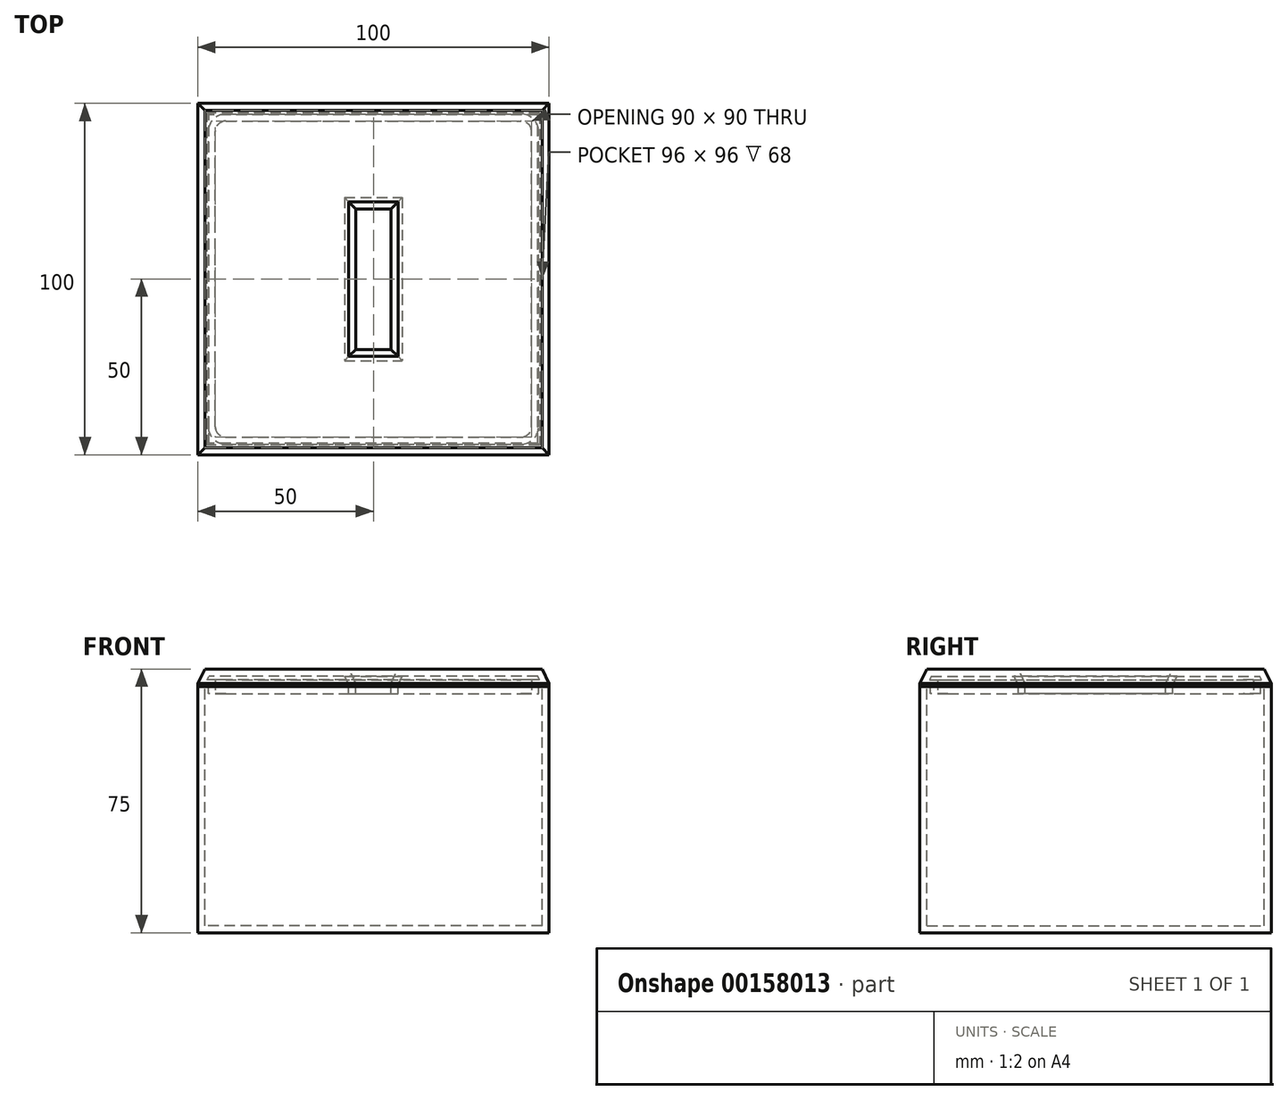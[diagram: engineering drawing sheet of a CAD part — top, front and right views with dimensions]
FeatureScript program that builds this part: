
annotation { "Feature Type Name" : "Feature", "Feature Type Description" : "" }
export const myFeature = defineFeature(function(context is Context, id is Id, definition is map)
    precondition{}
    {
        {
            var Q0;
            Q0=qCreatedBy(makeId("Top.planeOp"),FACE);
            var sketch = newSketch(context, id + "F0", { "sketchPlane" : qUnion([Q0])});
            skLineSegment(sketch, "E0.bottom", {"start": v(50, -50) * mm, "end": v(-50, -50) * mm});
            skLineSegment(sketch, "E0.top", {"start": v(50, 50) * mm, "end": v(-50, 50) * mm});
            skLineSegment(sketch, "E0.left", {"start": v(50, -50) * mm, "end": v(50, 50) * mm});
            skLineSegment(sketch, "E0.right", {"start": v(-50, -50) * mm, "end": v(-50, 50) * mm});
            skPoint(sketch, "E0.middle", {"position": v(0, 0) * mm});
            skSolve(sketch);
        }
        {
            var Q0;
            Q0=makeQuery(id+"F0.imprint","IMPRINT",FACE,{"disambiguationData":[TD([[makeQuery(id+"F0.imprint","IMPRINT",EDGE,{"derivedFrom":sQuery(id+"F0.wireOp",EDGE,"E0.bottom")}),-1.0]])]});
            extrude(context, id + "F1", {"entities" : qUnion([Q0]), "depth" : 70 * mm});
        }
        {
            var Q0;
            Q0=makeQuery(id+"F1.opExtrude","CAP_FACE",FACE,{"disambiguationData":[OSD([sQuery(id+"F0.wireOp",EDGE,"E0.bottom"),sQuery(id+"F0.wireOp",EDGE,"E0.top"),sQuery(id+"F0.wireOp",EDGE,"E0.left"),sQuery(id+"F0.wireOp",EDGE,"E0.right")])],"isStart":false});
            var sketch = newSketch(context, id + "F2", { "sketchPlane" : qUnion([Q0])});
            skLineSegment(sketch, "E1.bottom", {"start": v(48, -48) * mm, "end": v(-48, -48) * mm});
            skLineSegment(sketch, "E1.top", {"start": v(48, 48) * mm, "end": v(-48, 48) * mm});
            skLineSegment(sketch, "E1.left", {"start": v(48, -48) * mm, "end": v(48, 48) * mm});
            skLineSegment(sketch, "E1.right", {"start": v(-48, -48) * mm, "end": v(-48, 48) * mm});
            skPoint(sketch, "E1.middle", {"position": v(0, 0) * mm});
            skSolve(sketch);
        }
        {
            var Q0;
            Q0=makeQuery(id+"F2.imprint","IMPRINT",FACE,{"disambiguationData":[TD([[makeQuery(id+"F2.imprint","IMPRINT",EDGE,{"derivedFrom":sQuery(id+"F2.wireOp",EDGE,"E1.bottom")}),-1.0]])]});
            extrude(context, id + "F3", {"entities" : qUnion([Q0]), "operationType" : NewBodyOperationType.REMOVE, "oppositeDirection" : true, "depth" : 68 * mm});
        }
        {
            var Q0;
            Q0=makeQuery(id+"F1.opExtrude","CAP_FACE",FACE,{"disambiguationData":[OSD([sQuery(id+"F0.wireOp",EDGE,"E0.bottom"),sQuery(id+"F0.wireOp",EDGE,"E0.top"),sQuery(id+"F0.wireOp",EDGE,"E0.left"),sQuery(id+"F0.wireOp",EDGE,"E0.right")])],"isStart":false});
            var sketch = newSketch(context, id + "F4", { "sketchPlane" : qUnion([Q0])});
            skLineSegment(sketch, "E2.0", {"start": v(-50, -50) * mm, "end": v(-50, 50) * mm});
            skLineSegment(sketch, "E3.0", {"start": v(50, 50) * mm, "end": v(-50, 50) * mm});
            skLineSegment(sketch, "E3.1", {"start": v(50, -50) * mm, "end": v(50, 50) * mm});
            skLineSegment(sketch, "E3.2", {"start": v(50, -50) * mm, "end": v(-50, -50) * mm});
            skSolve(sketch);
        }
        {
            var Q0;
            Q0 = qSketchRegion(id + "F4", true);
            extrude(context, id + "F5", {"entities" : qUnion([Q0]), "depth" : 5 * mm});
        }
        {
            var Q0;
            Q0=makeQuery(id+"F5.opExtrude","CAP_FACE",FACE,{"disambiguationData":[OSD([sQuery(id+"F4.wireOp",EDGE,"E2.0"),sQuery(id+"F4.wireOp",EDGE,"E3.0"),sQuery(id+"F4.wireOp",EDGE,"E3.1"),sQuery(id+"F4.wireOp",EDGE,"E3.2")])],"isStart":true});
            var sketch = newSketch(context, id + "F6", { "sketchPlane" : qUnion([Q0])});
            skLineSegment(sketch, "E4.1", {"start": v(-48, 48) * mm, "end": v(-48, -48) * mm, "construction": true});
            skLineSegment(sketch, "E4.2", {"start": v(48, -48) * mm, "end": v(-48, -48) * mm, "construction": true});
            skLineSegment(sketch, "E4.3", {"start": v(48, 48) * mm, "end": v(48, -48) * mm, "construction": true});
            skLineSegment(sketch, "E4.4", {"start": v(48, 48) * mm, "end": v(-48, 48) * mm, "construction": true});
            skLineSegment(sketch, "E5.bottom", {"start": v(-47, 47) * mm, "end": v(47, 47) * mm});
            skLineSegment(sketch, "E5.top", {"start": v(-47, -47) * mm, "end": v(47, -47) * mm});
            skLineSegment(sketch, "E5.left", {"start": v(-47, 47) * mm, "end": v(-47, -47) * mm});
            skLineSegment(sketch, "E5.right", {"start": v(47, 47) * mm, "end": v(47, -47) * mm});
            skPoint(sketch, "E5.middle", {"position": v(0, 0) * mm});
            skSolve(sketch);
        }
        {
            var Q0;
            Q0=makeQuery(id+"F6.imprint","IMPRINT",FACE,{"disambiguationData":[TD([[makeQuery(id+"F6.imprint","IMPRINT",EDGE,{"derivedFrom":sQuery(id+"F6.wireOp",EDGE,"E5.bottom")}),-1.0]])]});
            extrude(context, id + "F7", {"entities" : qUnion([Q0]), "operationType" : NewBodyOperationType.ADD, "depth" : 2 * mm});
        }
        {
            var Q0;
            Q0=makeQuery(id+"F5.opExtrude","CAP_FACE",FACE,{"disambiguationData":[OSD([sQuery(id+"F4.wireOp",EDGE,"E2.0"),sQuery(id+"F4.wireOp",EDGE,"E3.0"),sQuery(id+"F4.wireOp",EDGE,"E3.1"),sQuery(id+"F4.wireOp",EDGE,"E3.2")])],"isStart":false});
            var sketch = newSketch(context, id + "F8", { "sketchPlane" : qUnion([Q0])});
            skLineSegment(sketch, "E6.bottom", {"start": v(5, -20) * mm, "end": v(-5, -20) * mm});
            skLineSegment(sketch, "E6.top", {"start": v(5, 20) * mm, "end": v(-5, 20) * mm});
            skLineSegment(sketch, "E6.left", {"start": v(5, -20) * mm, "end": v(5, 20) * mm});
            skLineSegment(sketch, "E6.right", {"start": v(-5, -20) * mm, "end": v(-5, 20) * mm});
            skPoint(sketch, "E6.middle", {"position": v(0, 0) * mm});
            skSolve(sketch);
        }
        {
            var Q0;
            Q0=makeQuery(id+"F8.imprint","IMPRINT",FACE,{"disambiguationData":[TD([[makeQuery(id+"F8.imprint","IMPRINT",EDGE,{"derivedFrom":sQuery(id+"F8.wireOp",EDGE,"E6.bottom")}),-1.0]])]});
            extrude(context, id + "F9", {"entities" : qUnion([Q0]), "operationType" : NewBodyOperationType.REMOVE, "oppositeDirection" : true, "depth" : 25 * mm});
        }
        {
            var Q0;
            Q0=makeQuery(id+"F7.opExtrude","SWEPT_EDGE",EDGE,{"disambiguationData":[OSD([sQuery(id+"F6.wireOp",EDGE,"E5.bottom"),sQuery(id+"F6.wireOp",EDGE,"E5.left")])]});
            var Q1;
            Q1=makeQuery(id+"F7.opExtrude","SWEPT_EDGE",EDGE,{"disambiguationData":[OSD([sQuery(id+"F6.wireOp",EDGE,"E5.bottom"),sQuery(id+"F6.wireOp",EDGE,"E5.right")])]});
            var Q2;
            Q2=makeQuery(id+"F7.opExtrude","SWEPT_EDGE",EDGE,{"disambiguationData":[OSD([sQuery(id+"F6.wireOp",EDGE,"E5.top"),sQuery(id+"F6.wireOp",EDGE,"E5.left")])]});
            var Q3;
            Q3=makeQuery(id+"F7.opExtrude","SWEPT_EDGE",EDGE,{"disambiguationData":[OSD([sQuery(id+"F6.wireOp",EDGE,"E5.top"),sQuery(id+"F6.wireOp",EDGE,"E5.right")])]});
            fillet(context, id + "F10", {"entities" : qUnion([Q0, Q1, Q2, Q3]), "radius" : 5 * mm, "tangentPropagation" : true, "allowEdgeOverflow" : false});
        }
        {
            var Q0;
            Q0=makeQuery(id+"F5.opExtrude","CAP_FACE",FACE,{"disambiguationData":[OSD([sQuery(id+"F4.wireOp",EDGE,"E2.0"),sQuery(id+"F4.wireOp",EDGE,"E3.0"),sQuery(id+"F4.wireOp",EDGE,"E3.1"),sQuery(id+"F4.wireOp",EDGE,"E3.2")])],"isStart":false});
            chamfer(context, id + "F11", {"entities" : qUnion([Q0]), "chamferType" : ChamferType.TWO_OFFSETS, "width1" : 4 * mm, "oppositeDirection" : false, "width2" : 2 * mm, "tangentPropagation" : true});
        }
        {
            var Q0;
            Q0=makeQuery(id+"F7.opExtrude","CAP_FACE",FACE,{"disambiguationData":[OSD([sQuery(id+"F6.wireOp",EDGE,"E5.bottom"),sQuery(id+"F6.wireOp",EDGE,"E5.top"),sQuery(id+"F6.wireOp",EDGE,"E5.left"),sQuery(id+"F6.wireOp",EDGE,"E5.right")])],"isStart":false});
            shell(context, id + "F12", {"entities" : qUnion([Q0]), "thickness" : 2 * mm});
        }
    });
